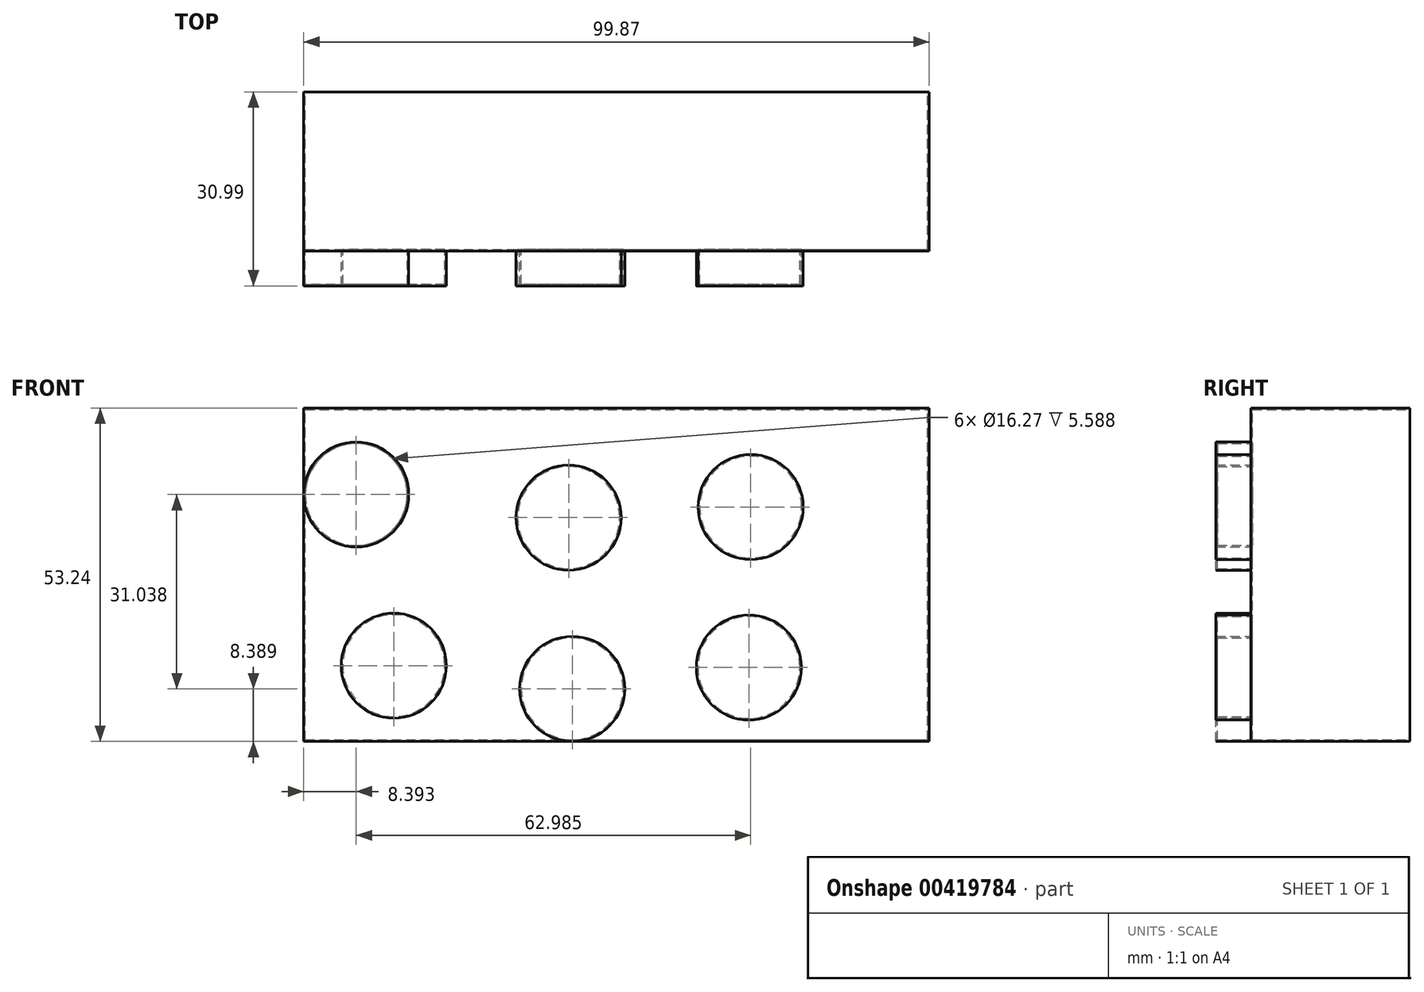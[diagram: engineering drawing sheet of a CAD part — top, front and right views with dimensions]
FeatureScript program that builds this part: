
annotation { "Feature Type Name" : "Feature", "Feature Type Description" : "" }
export const myFeature = defineFeature(function(context is Context, id is Id, definition is map)
    precondition{}
    {
        {
            var Q0;
            Q0=qCreatedBy(makeId("Front.planeOp"),FACE);
            var sketch = newSketch(context, id + "F0", { "sketchPlane" : qUnion([Q0])});
            skLineSegment(sketch, "E0.bottom", {"start": v(-47.49, -27.34) * mm, "end": v(52.38, -27.34) * mm});
            skLineSegment(sketch, "E0.top", {"start": v(-47.49, 25.9) * mm, "end": v(52.38, 25.9) * mm});
            skLineSegment(sketch, "E0.left", {"start": v(-47.49, -27.34) * mm, "end": v(-47.49, 25.9) * mm});
            skLineSegment(sketch, "E0.right", {"start": v(52.38, -27.34) * mm, "end": v(52.38, 25.9) * mm});
            skSolve(sketch);
        }
        {
            var Q0;
            Q0=makeQuery(id+"F0.imprint","IMPRINT",FACE,{"disambiguationData":[TD([[makeQuery(id+"F0.imprint","IMPRINT",EDGE,{"derivedFrom":sQuery(id+"F0.wireOp",EDGE,"E0.bottom")}),1.0]])]});
            extrude(context, id + "F1", {"entities" : qUnion([Q0]), "depth" : 25.4 * mm});
        }
        {
            var Q0;
            Q0=makeQuery(id+"F1.opExtrude","CAP_FACE",FACE,{"disambiguationData":[OSD([sQuery(id+"F0.wireOp",EDGE,"E0.bottom"),sQuery(id+"F0.wireOp",EDGE,"E0.top"),sQuery(id+"F0.wireOp",EDGE,"E0.left"),sQuery(id+"F0.wireOp",EDGE,"E0.right")])],"isStart":false});
            var sketch = newSketch(context, id + "F2", { "sketchPlane" : qUnion([Q0])});
            skCircle(sketch, "E1", {"center": v(-5.18, 8.4) * mm, "radius": 8.4 * mm});
            skCircle(sketch, "E2", {"center": v(23.89, 10.07) * mm, "radius": 8.4 * mm});
            skCircle(sketch, "E3", {"center": v(23.6, -15.54) * mm, "radius": 8.4 * mm});
            skCircle(sketch, "E4", {"center": v(-4.6, -18.95) * mm, "radius": 8.4 * mm});
            skCircle(sketch, "E5", {"center": v(-33.1, -15.25) * mm, "radius": 8.4 * mm});
            skCircle(sketch, "E6", {"center": v(-39.1, 12.09) * mm, "radius": 8.4 * mm});
            skLineSegment(sketch, "E7", {"start": v(52.38, 8.65) * mm, "end": v(-47.49, 8.65) * mm, "construction": true});
            skLineSegment(sketch, "E8", {"start": v(-47.49, 8.65) * mm, "end": v(52.38, 8.65) * mm, "construction": true});
            skLineSegment(sketch, "E9", {"start": v(52.38, -17.4) * mm, "end": v(-47.49, -27.34) * mm, "construction": true});
            skSolve(sketch);
        }
        {
            var Q0;
            Q0 = qSketchRegion(id + "F2", true);
            extrude(context, id + "F3", {"entities" : qUnion([Q0]), "operationType" : NewBodyOperationType.ADD, "depth" : 5.6 * mm});
        }
        {
            var Q0;
            Q0=makeQuery(id+"F1.opExtrude","CAP_FACE",FACE,{"disambiguationData":[OSD([sQuery(id+"F0.wireOp",EDGE,"E0.bottom"),sQuery(id+"F0.wireOp",EDGE,"E0.top"),sQuery(id+"F0.wireOp",EDGE,"E0.left"),sQuery(id+"F0.wireOp",EDGE,"E0.right")])],"isStart":true});
            shell(context, id + "F4", {"entities" : qUnion([Q0]), "thickness" : 0.25 * mm});
        }
    });
